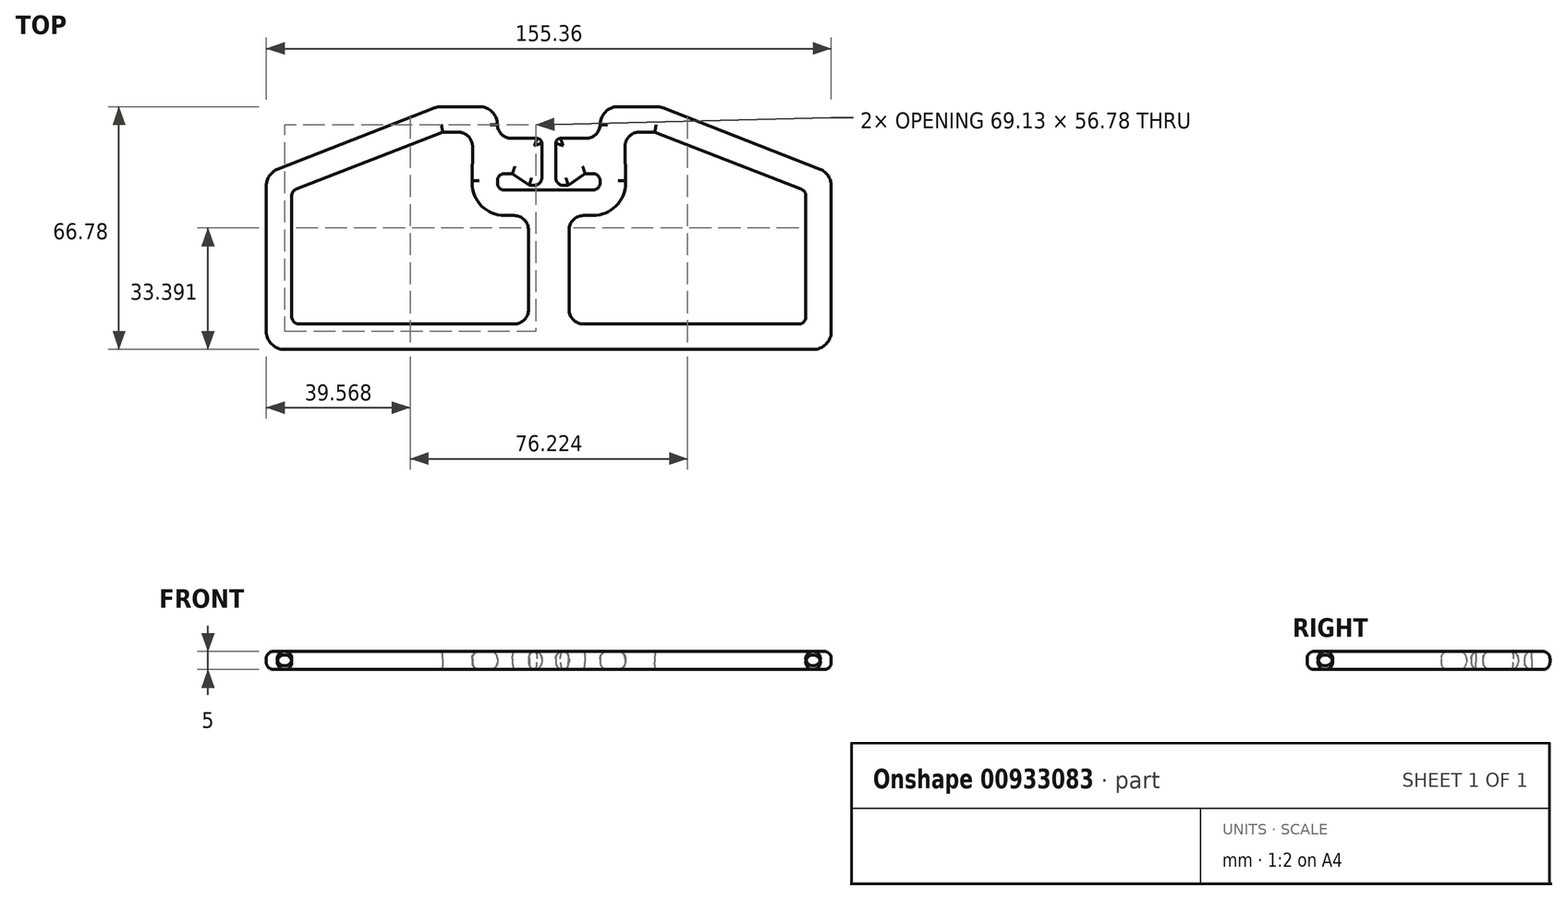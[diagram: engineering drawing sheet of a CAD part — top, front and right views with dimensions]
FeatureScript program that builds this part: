
annotation { "Feature Type Name" : "Feature", "Feature Type Description" : "" }
export const myFeature = defineFeature(function(context is Context, id is Id, definition is map)
    precondition{}
    {
        {
            var Q0;
            Q0=qCreatedBy(makeId("Top.planeOp"),FACE);
            var sketch = newSketch(context, id + "F0", { "sketchPlane" : qUnion([Q0])});
            skLineSegment(sketch, "E0", {"start": v(-74.5, 16.16) * mm, "end": v(-31.35, 33) * mm});
            skLineSegment(sketch, "E1", {"start": v(-29.53, 33.34) * mm, "end": v(-19.12, 33.34) * mm});
            skLineSegment(sketch, "E2", {"start": v(-10.22, 24.6) * mm, "end": v(-3.23, 24.6) * mm});
            skLineSegment(sketch, "E3", {"start": v(-1.92, 23.28) * mm, "end": v(-1.92, 13.7) * mm});
            skLineSegment(sketch, "E4", {"start": v(-3.92, 11.7) * mm, "end": v(-5.37, 11.7) * mm});
            skLineSegment(sketch, "E5", {"start": v(-5.37, 11.7) * mm, "end": v(-9.98, 14.92) * mm});
            skLineSegment(sketch, "E6", {"start": v(-9.98, 14.92) * mm, "end": v(-12.12, 14.92) * mm});
            skLineSegment(sketch, "E7", {"start": v(-14.12, 12.92) * mm, "end": v(-14.12, 12.37) * mm});
            skLineSegment(sketch, "E8", {"start": v(-12.12, 10.37) * mm, "end": v(0, 10.37) * mm});
            skLineSegment(sketch, "E9", {"start": v(-77.68, 11.5) * mm, "end": v(-77.68, -28.44) * mm});
            skLineSegment(sketch, "E10", {"start": v(-72.68, -33.44) * mm, "end": v(0, -33.44) * mm});
            skPoint(sketch, "E11.visualSharp", {"position": v(-77.68, 14.92) * mm});
            skArc(sketch, "E11.filletArc", {"start": v(-74.5, 16.16) * mm, "mid": v(-76.8, 14.32) * mm, "end": v(-77.68, 11.5) * mm});
            skPoint(sketch, "E12.visualSharp", {"position": v(-77.68, -33.44) * mm});
            skArc(sketch, "E12.filletArc", {"start": v(-77.68, -28.44) * mm, "mid": v(-76.21, -31.98) * mm, "end": v(-72.68, -33.44) * mm});
            skPoint(sketch, "E13.visualSharp", {"position": v(-30.47, 33.34) * mm});
            skArc(sketch, "E13.filletArc", {"start": v(-29.53, 33.34) * mm, "mid": v(-30.45, 33.25) * mm, "end": v(-31.35, 33) * mm});
            skPoint(sketch, "E14.visualSharp", {"position": v(-14.12, 33.34) * mm});
            skArc(sketch, "E14.filletArc", {"start": v(-14.12, 28.34) * mm, "mid": v(-15.59, 31.88) * mm, "end": v(-19.12, 33.34) * mm});
            skArc(sketch, "E15", {"start": v(-14.12, 28.34) * mm, "mid": v(-12.93, 25.68) * mm, "end": v(-10.22, 24.6) * mm});
            skPoint(sketch, "E16.visualSharp", {"position": v(-1.92, 24.6) * mm});
            skArc(sketch, "E16.filletArc", {"start": v(-1.92, 23.28) * mm, "mid": v(-2.3, 24.2) * mm, "end": v(-3.23, 24.6) * mm});
            skPoint(sketch, "E17.visualSharp", {"position": v(-1.92, 11.7) * mm});
            skArc(sketch, "E17.filletArc", {"start": v(-3.92, 11.7) * mm, "mid": v(-2.5, 12.28) * mm, "end": v(-1.92, 13.7) * mm});
            skPoint(sketch, "E18.visualSharp", {"position": v(-14.12, 14.92) * mm});
            skArc(sketch, "E18.filletArc", {"start": v(-12.12, 14.92) * mm, "mid": v(-13.54, 14.33) * mm, "end": v(-14.12, 12.92) * mm});
            skPoint(sketch, "E19.visualSharp", {"position": v(-14.12, 10.37) * mm});
            skArc(sketch, "E19.filletArc", {"start": v(-14.12, 12.37) * mm, "mid": v(-13.54, 10.96) * mm, "end": v(-12.12, 10.37) * mm});
            skArc(sketch, "E20.1", {"start": v(-21.12, 12.37) * mm, "mid": v(-18.49, 6.01) * mm, "end": v(-12.12, 3.37) * mm});
            skLineSegment(sketch, "E20.2", {"start": v(-21.12, 12.92) * mm, "end": v(-21.12, 12.37) * mm});
            skLineSegment(sketch, "E20.5", {"start": v(-68.68, -26.44) * mm, "end": v(-9.55, -26.44) * mm});
            skLineSegment(sketch, "E20.6", {"start": v(-70.68, 8.77) * mm, "end": v(-70.68, -24.44) * mm});
            skLineSegment(sketch, "E20.7", {"start": v(-69.4, 10.63) * mm, "end": v(-29.15, 26.34) * mm});
            skLineSegment(sketch, "E20.8", {"start": v(-29.15, 26.34) * mm, "end": v(-24.97, 26.34) * mm});
            skLineSegment(sketch, "E21", {"start": v(-20.97, 22.28) * mm, "end": v(-21.12, 12.92) * mm});
            skPoint(sketch, "E22.visualSharp", {"position": v(-20.9, 26.34) * mm});
            skArc(sketch, "E22.filletArc", {"start": v(-20.97, 22.28) * mm, "mid": v(-22.12, 25.15) * mm, "end": v(-24.97, 26.34) * mm});
            skPoint(sketch, "E23.visualSharp", {"position": v(-70.68, 10.14) * mm});
            skArc(sketch, "E23.filletArc", {"start": v(-69.4, 10.63) * mm, "mid": v(-70.33, 9.9) * mm, "end": v(-70.68, 8.77) * mm});
            skPoint(sketch, "E24.visualSharp", {"position": v(-70.68, -26.44) * mm});
            skArc(sketch, "E24.filletArc", {"start": v(-70.68, -24.44) * mm, "mid": v(-70.09, -25.85) * mm, "end": v(-68.68, -26.44) * mm});
            skLineSegment(sketch, "E25", {"start": v(-5.55, -0.63) * mm, "end": v(-5.55, -22.44) * mm});
            skLineSegment(sketch, "E26", {"start": v(-12.12, 3.37) * mm, "end": v(-9.55, 3.37) * mm});
            skPoint(sketch, "E27.visualSharp", {"position": v(-5.55, 3.37) * mm});
            skArc(sketch, "E27.filletArc", {"start": v(-5.55, -0.63) * mm, "mid": v(-6.72, 2.2) * mm, "end": v(-9.55, 3.37) * mm});
            skArc(sketch, "E28.filletArc", {"start": v(-9.55, -26.44) * mm, "mid": v(-6.72, -25.27) * mm, "end": v(-5.55, -22.44) * mm});
            skLineSegment(sketch, "E29", {"start": v(0, 10.37) * mm, "end": v(0, -33.44) * mm});
            skSolve(sketch);
        }
        {
            var Q0;
            Q0=makeQuery(id+"F0.imprint","IMPRINT",FACE,{"disambiguationData":[TD([[makeQuery(id+"F0.imprint","IMPRINT",EDGE,{"derivedFrom":sQuery(id+"F0.wireOp",EDGE,"E0")}),-1.0]])]});
            extrude(context, id + "F1", {"entities" : qUnion([Q0]), "depth" : 5 * mm, "offsetDistance" : 25 * mm});
        }
        {
            var Q0;
            Q0=makeQuery(id+"F1.opExtrude","SWEPT_BODY",BODY,{"disambiguationData":[OSD([sQuery(id+"F0.wireOp",EDGE,"E0"),sQuery(id+"F0.wireOp",EDGE,"E1"),sQuery(id+"F0.wireOp",EDGE,"E2"),sQuery(id+"F0.wireOp",EDGE,"E3"),sQuery(id+"F0.wireOp",EDGE,"E4"),sQuery(id+"F0.wireOp",EDGE,"E5"),sQuery(id+"F0.wireOp",EDGE,"E6"),sQuery(id+"F0.wireOp",EDGE,"E7"),sQuery(id+"F0.wireOp",EDGE,"E8"),sQuery(id+"F0.wireOp",EDGE,"E9"),sQuery(id+"F0.wireOp",EDGE,"E10"),sQuery(id+"F0.wireOp",EDGE,"E11.filletArc"),sQuery(id+"F0.wireOp",EDGE,"E12.filletArc"),sQuery(id+"F0.wireOp",EDGE,"E13.filletArc"),sQuery(id+"F0.wireOp",EDGE,"E14.filletArc"),sQuery(id+"F0.wireOp",EDGE,"E15"),sQuery(id+"F0.wireOp",EDGE,"E16.filletArc"),sQuery(id+"F0.wireOp",EDGE,"E17.filletArc"),sQuery(id+"F0.wireOp",EDGE,"E18.filletArc"),sQuery(id+"F0.wireOp",EDGE,"E19.filletArc"),sQuery(id+"F0.wireOp",EDGE,"E20.1"),sQuery(id+"F0.wireOp",EDGE,"E20.2"),sQuery(id+"F0.wireOp",EDGE,"E20.5"),sQuery(id+"F0.wireOp",EDGE,"E20.6"),sQuery(id+"F0.wireOp",EDGE,"E20.7"),sQuery(id+"F0.wireOp",EDGE,"E20.8"),sQuery(id+"F0.wireOp",EDGE,"E21"),sQuery(id+"F0.wireOp",EDGE,"E22.filletArc"),sQuery(id+"F0.wireOp",EDGE,"E23.filletArc"),sQuery(id+"F0.wireOp",EDGE,"E24.filletArc"),sQuery(id+"F0.wireOp",EDGE,"E25"),sQuery(id+"F0.wireOp",EDGE,"E26"),sQuery(id+"F0.wireOp",EDGE,"E27.filletArc"),sQuery(id+"F0.wireOp",EDGE,"E28.filletArc"),sQuery(id+"F0.wireOp",EDGE,"E29")])]});
            var Q1;
            Q1=makeQuery(id+"F1.opExtrude","SWEPT_FACE",FACE,{"disambiguationData":[OSD([sQuery(id+"F0.wireOp",EDGE,"E29")])]});
            mirror(context, id + "F2", {"operationType" : NewBodyOperationType.ADD, "entities" : qUnion([Q0]), "mirrorPlane" : qUnion([Q1])});
        }
        {
            var Q0;
            {var subQ0=makeQuery(id+"F1.opExtrude","CAP_FACE",FACE,{"disambiguationData":[OSD([sQuery(id+"F0.wireOp",EDGE,"E0"),sQuery(id+"F0.wireOp",EDGE,"E1"),sQuery(id+"F0.wireOp",EDGE,"E2"),sQuery(id+"F0.wireOp",EDGE,"E3"),sQuery(id+"F0.wireOp",EDGE,"E4"),sQuery(id+"F0.wireOp",EDGE,"E5"),sQuery(id+"F0.wireOp",EDGE,"E6"),sQuery(id+"F0.wireOp",EDGE,"E7"),sQuery(id+"F0.wireOp",EDGE,"E8"),sQuery(id+"F0.wireOp",EDGE,"E9"),sQuery(id+"F0.wireOp",EDGE,"E10"),sQuery(id+"F0.wireOp",EDGE,"E11.filletArc"),sQuery(id+"F0.wireOp",EDGE,"E12.filletArc"),sQuery(id+"F0.wireOp",EDGE,"E13.filletArc"),sQuery(id+"F0.wireOp",EDGE,"E14.filletArc"),sQuery(id+"F0.wireOp",EDGE,"E15"),sQuery(id+"F0.wireOp",EDGE,"E16.filletArc"),sQuery(id+"F0.wireOp",EDGE,"E17.filletArc"),sQuery(id+"F0.wireOp",EDGE,"E18.filletArc"),sQuery(id+"F0.wireOp",EDGE,"E19.filletArc"),sQuery(id+"F0.wireOp",EDGE,"E20.1"),sQuery(id+"F0.wireOp",EDGE,"E20.2"),sQuery(id+"F0.wireOp",EDGE,"E20.5"),sQuery(id+"F0.wireOp",EDGE,"E20.6"),sQuery(id+"F0.wireOp",EDGE,"E20.7"),sQuery(id+"F0.wireOp",EDGE,"E20.8"),sQuery(id+"F0.wireOp",EDGE,"E21"),sQuery(id+"F0.wireOp",EDGE,"E22.filletArc"),sQuery(id+"F0.wireOp",EDGE,"E23.filletArc"),sQuery(id+"F0.wireOp",EDGE,"E24.filletArc"),sQuery(id+"F0.wireOp",EDGE,"E25"),sQuery(id+"F0.wireOp",EDGE,"E26"),sQuery(id+"F0.wireOp",EDGE,"E27.filletArc"),sQuery(id+"F0.wireOp",EDGE,"E28.filletArc"),sQuery(id+"F0.wireOp",EDGE,"E29")])],"isStart":false});Q0=makeQuery(id+"F2.boolean.opBoolean","MERGE",FACE,{"derivedFrom":[subQ0,makeQuery(id+"F2.opPattern","COPY",FACE,{"derivedFrom":subQ0,"instanceName":"1"})]});}
            var Q1;
            {var subQ0=makeQuery(id+"F1.opExtrude","CAP_FACE",FACE,{"disambiguationData":[OSD([sQuery(id+"F0.wireOp",EDGE,"E0"),sQuery(id+"F0.wireOp",EDGE,"E1"),sQuery(id+"F0.wireOp",EDGE,"E2"),sQuery(id+"F0.wireOp",EDGE,"E3"),sQuery(id+"F0.wireOp",EDGE,"E4"),sQuery(id+"F0.wireOp",EDGE,"E5"),sQuery(id+"F0.wireOp",EDGE,"E6"),sQuery(id+"F0.wireOp",EDGE,"E7"),sQuery(id+"F0.wireOp",EDGE,"E8"),sQuery(id+"F0.wireOp",EDGE,"E9"),sQuery(id+"F0.wireOp",EDGE,"E10"),sQuery(id+"F0.wireOp",EDGE,"E11.filletArc"),sQuery(id+"F0.wireOp",EDGE,"E12.filletArc"),sQuery(id+"F0.wireOp",EDGE,"E13.filletArc"),sQuery(id+"F0.wireOp",EDGE,"E14.filletArc"),sQuery(id+"F0.wireOp",EDGE,"E15"),sQuery(id+"F0.wireOp",EDGE,"E16.filletArc"),sQuery(id+"F0.wireOp",EDGE,"E17.filletArc"),sQuery(id+"F0.wireOp",EDGE,"E18.filletArc"),sQuery(id+"F0.wireOp",EDGE,"E19.filletArc"),sQuery(id+"F0.wireOp",EDGE,"E20.1"),sQuery(id+"F0.wireOp",EDGE,"E20.2"),sQuery(id+"F0.wireOp",EDGE,"E20.5"),sQuery(id+"F0.wireOp",EDGE,"E20.6"),sQuery(id+"F0.wireOp",EDGE,"E20.7"),sQuery(id+"F0.wireOp",EDGE,"E20.8"),sQuery(id+"F0.wireOp",EDGE,"E21"),sQuery(id+"F0.wireOp",EDGE,"E22.filletArc"),sQuery(id+"F0.wireOp",EDGE,"E23.filletArc"),sQuery(id+"F0.wireOp",EDGE,"E24.filletArc"),sQuery(id+"F0.wireOp",EDGE,"E25"),sQuery(id+"F0.wireOp",EDGE,"E26"),sQuery(id+"F0.wireOp",EDGE,"E27.filletArc"),sQuery(id+"F0.wireOp",EDGE,"E28.filletArc"),sQuery(id+"F0.wireOp",EDGE,"E29")])],"isStart":true});Q1=makeQuery(id+"F2.boolean.opBoolean","MERGE",FACE,{"derivedFrom":[subQ0,makeQuery(id+"F2.opPattern","COPY",FACE,{"derivedFrom":subQ0,"instanceName":"1"})]});}
            fillet(context, id + "F3", {"entities" : qUnion([Q0, Q1]), "radius" : 2 * mm, "tangentPropagation" : true, "allowEdgeOverflow" : false});
        }
    });
